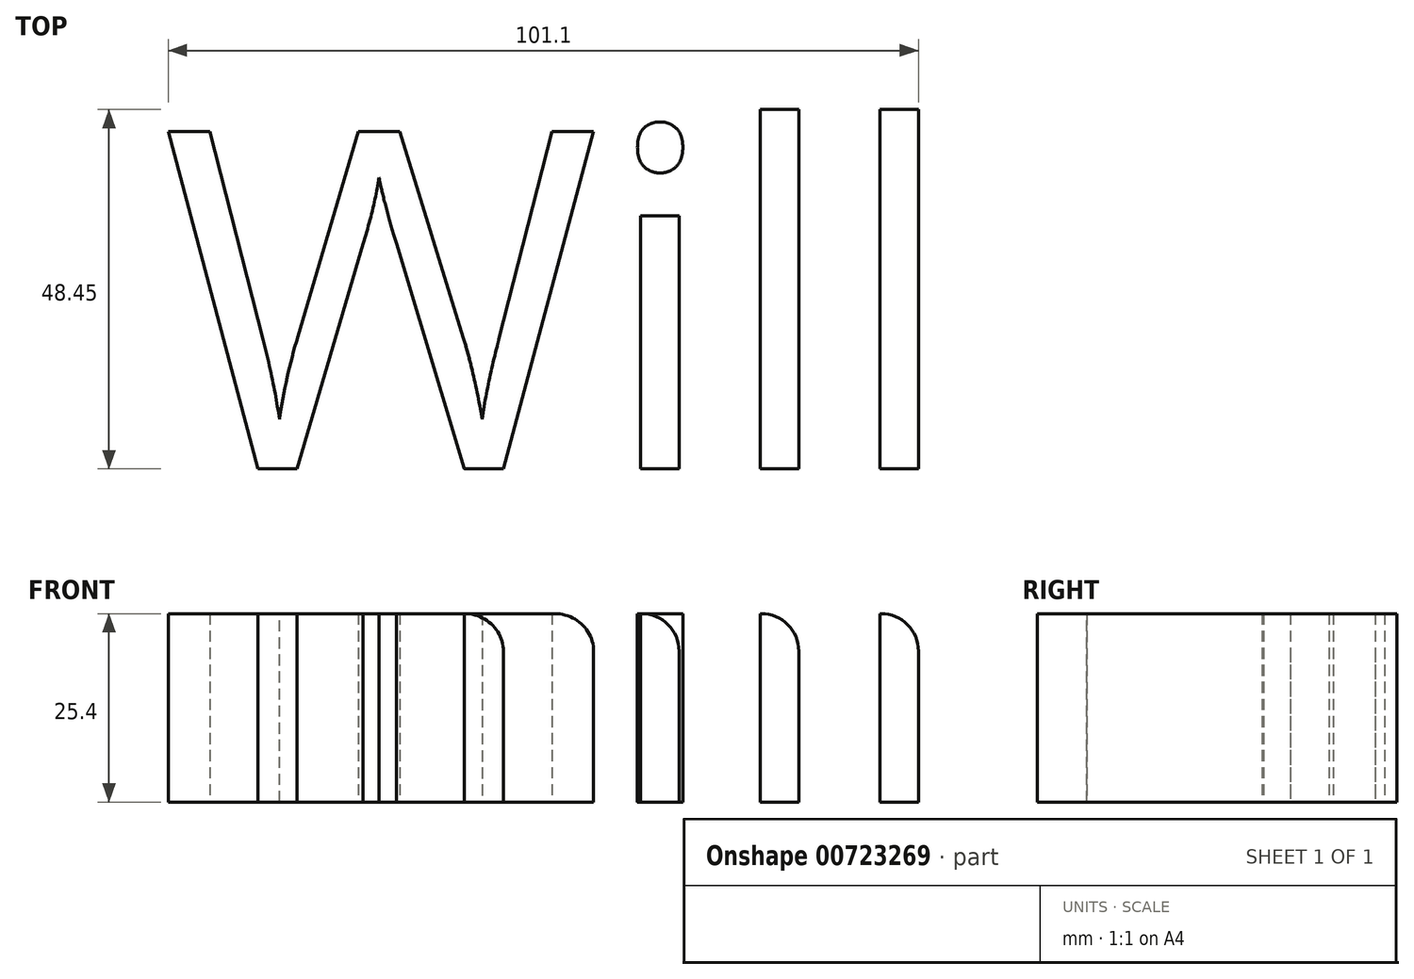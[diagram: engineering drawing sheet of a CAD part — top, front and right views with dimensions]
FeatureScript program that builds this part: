
annotation { "Feature Type Name" : "Feature", "Feature Type Description" : "" }
export const myFeature = defineFeature(function(context is Context, id is Id, definition is map)
    precondition{}
    {
        {
            var Q0;
            Q0=qCreatedBy(makeId("Top.planeOp"),FACE);
            var sketch = newSketch(context, id + "F0", { "sketchPlane" : qUnion([Q0])});
            skText(sketch, "E0", { "text": "Will", "fontName": "OpenSans-Regular.ttf"});
            const initialGuessF0  = {"E0": [-0.10608, -0.04591, 1, 0, 0.04591]};
            skSetInitialGuess(sketch, initialGuessF0);
            skSolve(sketch);
        }
        {
            var Q0;
            Q0 = qSketchRegion(id + "F0", true);
            extrude(context, id + "F1", {"entities" : qUnion([Q0]), "depth" : 25.4 * mm, "offsetDistance" : 25.4 * mm});
        }
        {
            var Q0;
            Q0=makeQuery(id+"F1.opExtrude","CAP_EDGE",EDGE,{"disambiguationData":[OSD([sQuery(id+"F0.wireOp",EDGE,"E0.sketch_text.stroke-39")])],"isStart":false});
            var Q1;
            Q1=makeQuery(id+"F1.opExtrude","CAP_EDGE",EDGE,{"disambiguationData":[OSD([sQuery(id+"F0.wireOp",EDGE,"E0.sketch_text.stroke-35")])],"isStart":false});
            var Q2;
            Q2=makeQuery(id+"F1.opExtrude","CAP_EDGE",EDGE,{"disambiguationData":[OSD([sQuery(id+"F0.wireOp",EDGE,"E0.sketch_text.stroke-23")])],"isStart":false});
            var Q3;
            Q3=makeQuery(id+"F1.opExtrude","SWEPT_EDGE",EDGE,{"disambiguationData":[OSD([sQuery(id+"F0.wireOp",EDGE,"E0.sketch_text.stroke-28"),sQuery(id+"F0.wireOp",EDGE,"E0.sketch_text.stroke-29")])]});
            var Q4;
            Q4=makeQuery(id+"F1.opExtrude","SWEPT_EDGE",EDGE,{"disambiguationData":[OSD([sQuery(id+"F0.wireOp",EDGE,"E0.sketch_text.stroke-27"),sQuery(id+"F0.wireOp",EDGE,"E0.sketch_text.stroke-28")])]});
            var Q5;
            Q5=makeQuery(id+"F1.opExtrude","CAP_EDGE",EDGE,{"disambiguationData":[OSD([sQuery(id+"F0.wireOp",EDGE,"E0.sketch_text.stroke-19")])],"isStart":false});
            fillet(context, id + "F2", {"entities" : qUnion([Q0, Q1, Q2, Q3, Q4, Q5]), "radius" : 5.08 * mm, "tangentPropagation" : true, "allowEdgeOverflow" : false});
        }
    });
